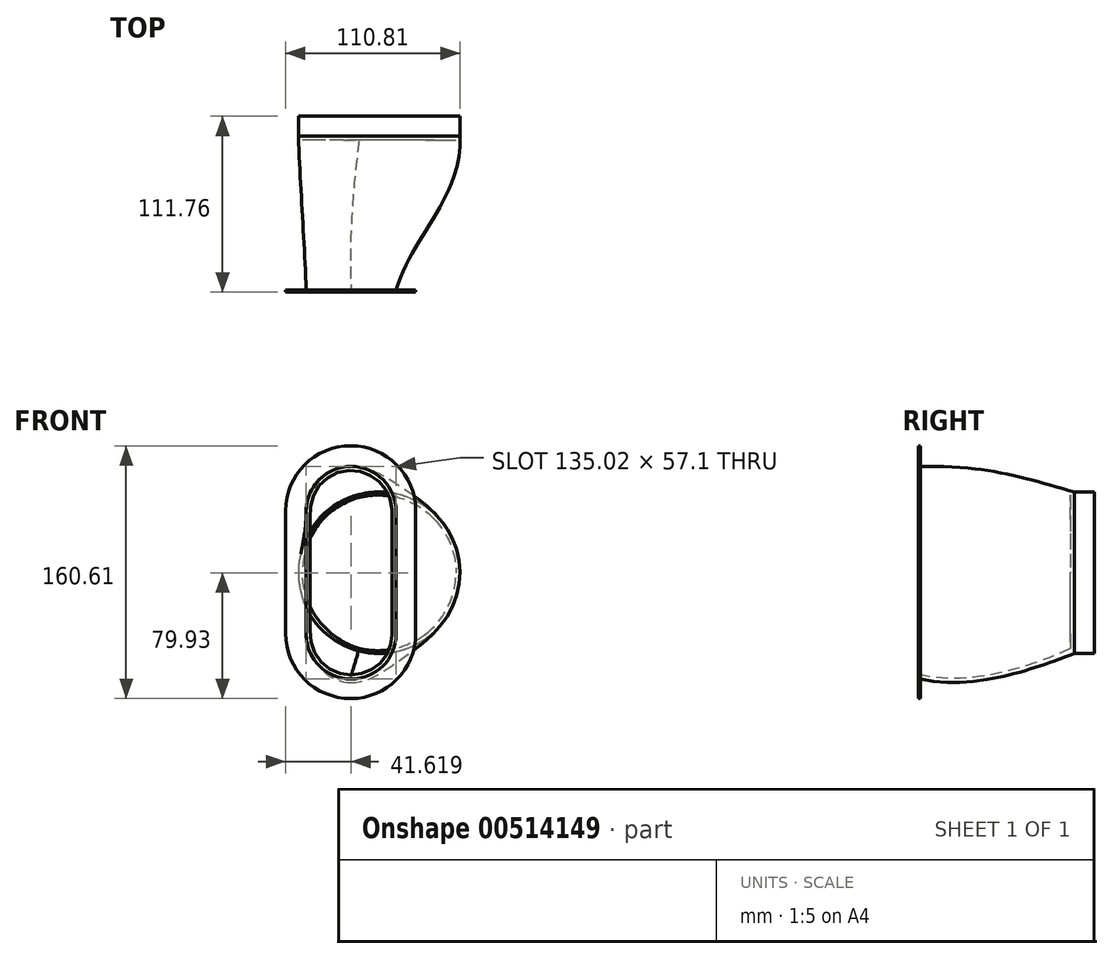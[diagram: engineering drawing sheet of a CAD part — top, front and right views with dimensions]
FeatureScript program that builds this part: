
annotation { "Feature Type Name" : "Feature", "Feature Type Description" : "" }
export const myFeature = defineFeature(function(context is Context, id is Id, definition is map)
    precondition{}
    {
        {
            var Q0;
            Q0=qCreatedBy(makeId("Front.planeOp"),FACE);
            var sketch = newSketch(context, id + "F0", { "sketchPlane" : qUnion([Q0])});
            skCircle(sketch, "E0", {"center": v(0, 0) * mm, "radius": 51.26 * mm});
            skSolve(sketch);
        }
        {
            var Q0;
            Q0=qCreatedBy(makeId("Front.planeOp"),FACE);
            cPlane(context, id + "F1", {"entities" : qUnion([Q0]), "cplaneType" : CPlaneType.OFFSET, "offset" : 110.49 * mm, "width" : 152.4 * mm, "height" : 152.4 * mm});
        }
        {
            var Q0;
            Q0=qCreatedBy(id+"F1.planeOp",FACE);
            var sketch = newSketch(context, id + "F2", { "sketchPlane" : qUnion([Q0])});
            skLineSegment(sketch, "E1.left", {"start": v(10.79, 38.96) * mm, "end": v(10.79, -38.96) * mm});
            skLineSegment(sketch, "E1.right", {"start": v(-46.3, 38.96) * mm, "end": v(-46.3, -38.96) * mm});
            skPoint(sketch, "E1.middle", {"position": v(-17.76, 0) * mm});
            skArc(sketch, "E2", {"start": v(10.79, 38.96) * mm, "mid": v(-17.76, 67.51) * mm, "end": v(-46.3, 38.96) * mm});
            skArc(sketch, "E3", {"start": v(-46.3, -38.96) * mm, "mid": v(-17.76, -67.51) * mm, "end": v(10.79, -38.96) * mm});
            skLineSegment(sketch, "E4", {"start": v(-17.76, 67.51) * mm, "end": v(-17.76, -67.51) * mm, "construction": true});
            skLineSegment(sketch, "E5", {"start": v(-46.3, 38.96) * mm, "end": v(10.79, 38.96) * mm, "construction": true});
            skLineSegment(sketch, "E6", {"start": v(-46.3, -38.96) * mm, "end": v(10.79, -38.96) * mm, "construction": true});
            skLineSegment(sketch, "E7.left", {"start": v(23.3, 39.34) * mm, "end": v(23.3, -38.58) * mm});
            skLineSegment(sketch, "E7.right", {"start": v(-59.38, 39.34) * mm, "end": v(-59.38, -38.58) * mm});
            skArc(sketch, "E8", {"start": v(23.3, 39.34) * mm, "mid": v(-18.04, 80.68) * mm, "end": v(-59.38, 39.34) * mm});
            skArc(sketch, "E9", {"start": v(-59.38, -38.58) * mm, "mid": v(-18.04, -79.93) * mm, "end": v(23.3, -38.58) * mm});
            skSolve(sketch);
        }
        {
            var Q0;
            Q0=makeQuery(id+"F0.imprint","IMPRINT",FACE,{"disambiguationData":[TD([[makeQuery(id+"F0.imprint","IMPRINT",EDGE,{"derivedFrom":sQuery(id+"F0.wireOp",EDGE,"E0")}),1.0]])]});
            extrude(context, id + "F3", {"entities" : qUnion([Q0]), "depth" : 12.7 * mm});
        }
        {
            var Q0;
            Q0=makeQuery(id+"F3.opExtrude","CAP_FACE",FACE,{"disambiguationData":[OSD([sQuery(id+"F0.wireOp",EDGE,"E0")])],"isStart":false});
            var sketch = newSketch(context, id + "F4", { "sketchPlane" : qUnion([Q0])});
            skArc(sketch, "E10", {"start": v(-45, 24.54) * mm, "mid": v(-49.01, -15) * mm, "end": v(-23.55, -45.53) * mm});
            skArc(sketch, "E11", {"start": v(36.96, 35.52) * mm, "mid": v(-6.8, 50.8) * mm, "end": v(-45, 24.54) * mm});
            skArc(sketch, "E12", {"start": v(31.02, -40.8) * mm, "mid": v(51.1, -3.98) * mm, "end": v(36.96, 35.52) * mm});
            skArc(sketch, "E13", {"start": v(-23.55, -45.53) * mm, "mid": v(4.42, -51.07) * mm, "end": v(31.02, -40.8) * mm});
            skSolve(sketch);
        }
        {
            var Q0;
            Q0=qCreatedBy(makeId("Top.planeOp"),FACE);
            var sketch = newSketch(context, id + "F5", { "sketchPlane" : qUnion([Q0])});
            skFitSpline(sketch, "E14", {"points": [v(51.26, -12.7) * mm, v(10.79, -110.5) * mm], "startDerivative": vector(8.6, -111.1) * mm, "endDerivative": vector(-26.23, -97) * mm});
            skFitSpline(sketch, "E15", {"points": [v(-51.26, -12.7) * mm, v(-46.3, -110.5) * mm], "startDerivative": vector(3.47, -97.02) * mm, "endDerivative": vector(3.47, -97.02) * mm});
            skFitSpline(sketch, "E16", {"points": [v(-51.26, -12.7) * mm, v(51.26, -12.7) * mm], "startDerivative": vector(102.52, 0) * mm, "endDerivative": vector(102.52, 0) * mm});
            skFitSpline(sketch, "E17", {"points": [v(10.79, -110.5) * mm, v(-46.3, -110.5) * mm], "startDerivative": vector(-57.1, 0) * mm, "endDerivative": vector(-57.1, 0) * mm});
            skSolve(sketch);
        }
        {
            var Q0;
            Q0=sQuery(id+"F2.wireOp",EDGE,"E2");
            cPoint(context, id + "F6", {"entities" : qUnion([Q0]), "parameter" : 0.5});
        }
        {
            var Q0;
            Q0=sQuery(id+"F4.wireOp",EDGE,"E11");
            var Q1;
            Q1 = qCreatedBy(id + "F6" ,VERTEX);
            cPlane(context, id + "F7", {"entities" : qUnion([Q0, Q1]), "cplaneType" : CPlaneType.CURVE_POINT, "offset" : 25.4 * mm, "width" : 152.4 * mm, "height" : 152.4 * mm});
        }
        {
            var Q0;
            Q0=qCreatedBy(id+"F7.planeOp",FACE);
            var sketch = newSketch(context, id + "F8", { "sketchPlane" : qUnion([Q0])});
            skFitSpline(sketch, "E18", {"points": [v(110.5, 69.8) * mm, v(12.7, 51.26) * mm], "startDerivative": vector(-109.14, 3.64) * mm, "endDerivative": vector(-103.66, -37.1) * mm});
            skSolve(sketch);
        }
        {
            var Q0;
            Q0=sQuery(id+"F4.wireOp",EDGE,"E13");
            var Q1;
            Q1=sQuery(id+"F2.wireOp",VERTEX,"E4.end");
            cPlane(context, id + "F9", {"entities" : qUnion([Q0, Q1]), "cplaneType" : CPlaneType.CURVE_POINT, "offset" : 25.4 * mm, "width" : 152.4 * mm, "height" : 152.4 * mm});
        }
        {
            var Q0;
            Q0=qCreatedBy(id+"F9.planeOp",FACE);
            var sketch = newSketch(context, id + "F10", { "sketchPlane" : qUnion([Q0])});
            skFitSpline(sketch, "E19", {"points": [v(-110.5, -69.8) * mm, v(-12.7, -51.26) * mm], "startDerivative": vector(77.51, -18.77) * mm, "endDerivative": vector(105.52, 52.75) * mm});
            skSolve(sketch);
        }
        {
            var Q0;
            Q0 = qSketchRegion(id + "F4", true);
            var Q1;
            Q1=makeQuery(id+"F2.imprint","IMPRINT",FACE,{"disambiguationData":[TD([[makeQuery(id+"F2.imprint","IMPRINT",EDGE,{"derivedFrom":sQuery(id+"F2.wireOp",EDGE,"E1.left")}),-1.0]])]});
            var Q2;
            Q2=sQuery(id+"F5.wireOp",EDGE,"E15");
            var Q3;
            Q3=sQuery(id+"F8.wireOp",EDGE,"E18");
            var Q4;
            Q4=sQuery(id+"F10.wireOp",EDGE,"E19");
            var Q5;
            Q5=sQuery(id+"F5.wireOp",EDGE,"E14");
            loft(context, id + "F11", {"addGuides" : true, "sheetProfilesArray" : [{ "sheetProfileEntities" : qUnion([Q0]) }, { "sheetProfileEntities" : qUnion([Q1]) }], "guidesArray" : [{ "guideEntities" : qUnion([Q2]), "guideDerivativeType" : LoftGuideDerivativeType.DEFAULT, "guideDerivativeMagnitude" : 1 }, { "guideEntities" : qUnion([Q3]), "guideDerivativeType" : LoftGuideDerivativeType.DEFAULT, "guideDerivativeMagnitude" : 1 }, { "guideEntities" : qUnion([Q4]), "guideDerivativeType" : LoftGuideDerivativeType.DEFAULT, "guideDerivativeMagnitude" : 1 }, { "guideEntities" : qUnion([Q5]), "guideDerivativeType" : LoftGuideDerivativeType.DEFAULT, "guideDerivativeMagnitude" : 1 }]});
        }
        {
            var Q0;
            Q0=makeQuery(id+"F11.opLoft","CAP_FACE",FACE,{"disambiguationData":[OSD([makeQuery(id+"F2.imprint","IMPRINT",FACE,{"disambiguationData":[TD([[makeQuery(id+"F2.imprint","IMPRINT",EDGE,{"derivedFrom":sQuery(id+"F2.wireOp",EDGE,"E1.left")}),-1.0]])]})])],"isStart":true});
            shell(context, id + "F12", {"entities" : qUnion([Q0]), "thickness" : 2.54 * mm});
        }
        {
            var Q0;
            Q0=makeQuery(id+"F2.imprint","IMPRINT",FACE,{"disambiguationData":[TD([[makeQuery(id+"F2.imprint","IMPRINT",EDGE,{"derivedFrom":sQuery(id+"F2.wireOp",EDGE,"E1.left")}),1.0]])]});
            var Q1;
            Q1=sQuery(id+"F2.wireOp",EDGE,"E7.left");
            var Q2;
            Q2=sQuery(id+"F2.wireOp",EDGE,"E7.right");
            var Q3;
            Q3=sQuery(id+"F2.wireOp",EDGE,"E9");
            var Q4;
            Q4=sQuery(id+"F2.wireOp",EDGE,"E8");
            extrude(context, id + "F13", {"entities" : qUnion([Q0]), "surfaceEntities" : qUnion([Q1, Q2, Q3, Q4]), "depth" : 1.27 * mm, "offsetDistance" : 25.4 * mm});
        }
    });
